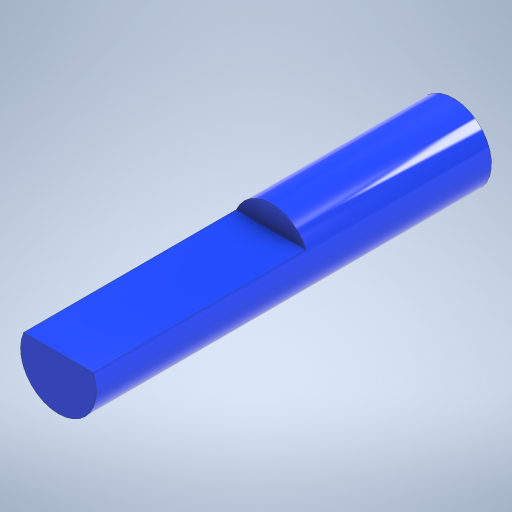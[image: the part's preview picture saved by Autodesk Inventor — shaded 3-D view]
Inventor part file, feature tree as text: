
AUTODESK INVENTOR PART (.ipt)
format: ipt  version: 2023.2 (Build 272271030, 271C)  size: 248,320 bytes
history: native  units: mm
features: extrude x2, sketch x1
ambient origin geometry x8: Origin, YZ Plane, XZ Plane, XY Plane, X Axis, Y Axis, Z Axis, Center Point
bodies: Solid1 (feature_tree)
feature tree (3):
  sketch  "Sketch1"  dims[d0=5.0mm d1=1.0mm d2=26.0mm d3=0.0mm d4=12.0mm d5=0.0mm]
  extrude  "Extrusion1"  Depth=12.0mm
  extrude  "Extrusion2"  Depth=26.0mm TaperAngle=0.0deg
